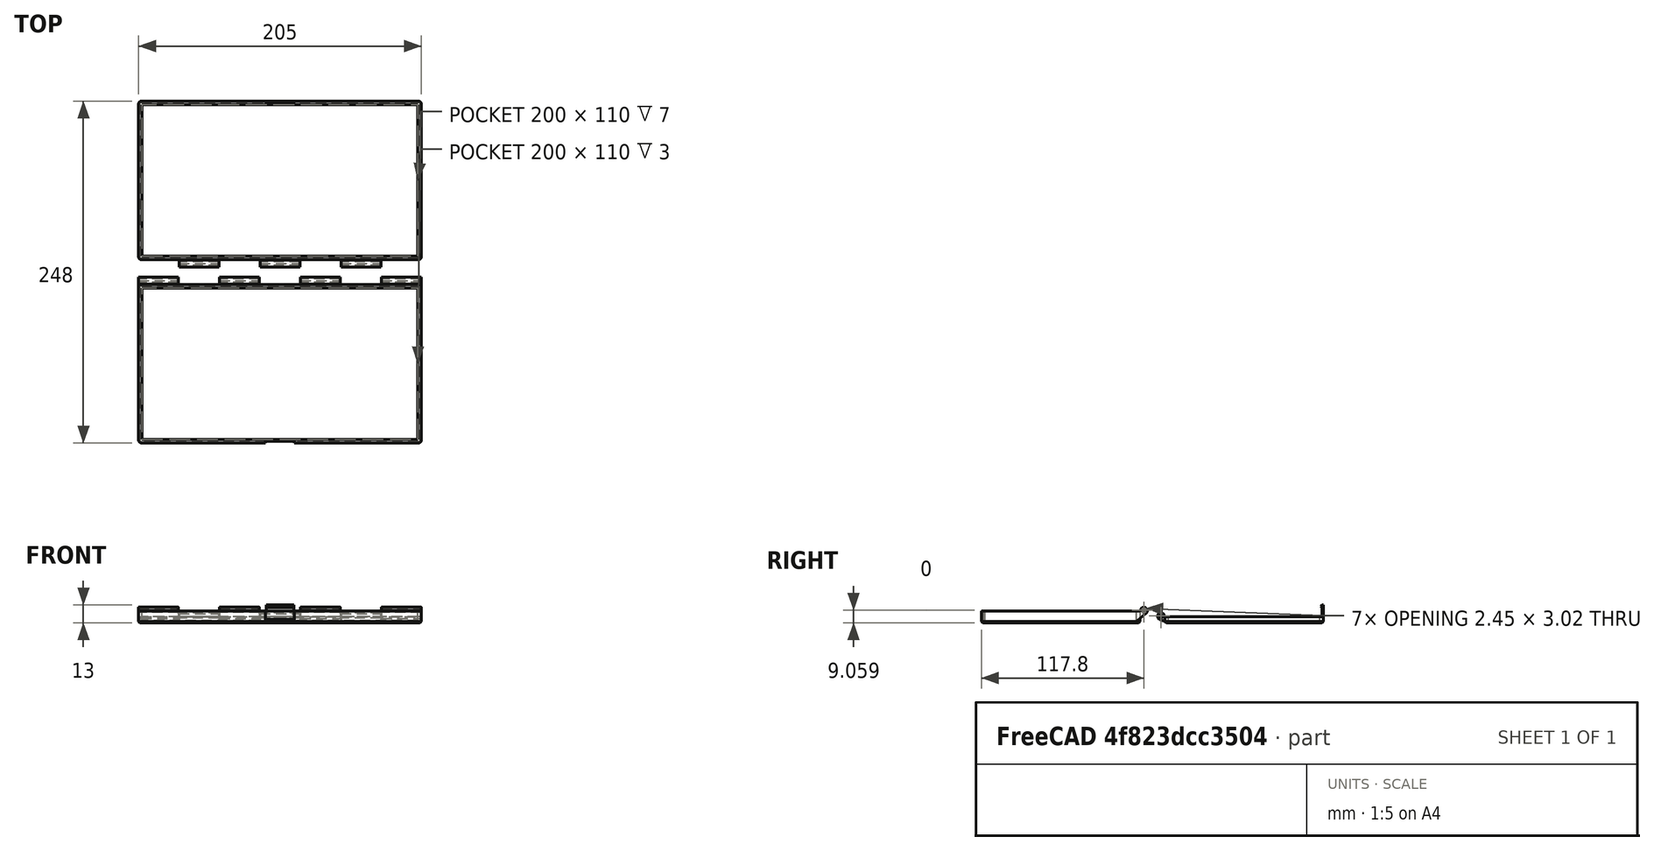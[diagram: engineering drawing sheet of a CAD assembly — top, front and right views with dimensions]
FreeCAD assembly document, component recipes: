
FREECAD ASSEMBLY — COMPONENT RECIPES ("parametric box")

This assembly document has 2 components, labeled P0..P1 below (a component is one placed body or linked part). 2 of them carry a construction recipe — the FreeCAD feature program that regenerates the part from scratch, quoted from this document or its linked companion documents; the rest are supplied as boundary geometry only. No exploded tour is included for this assembly.
COMPONENT P0 — recipe-attached ("bottom", modeled in this document).
Construction recipe (the document's own serialized feature program — sketch geometry with constraints, then the solid features built on it; lengths are millimeters unless a unit is written):

FEATURE [Sketcher::SketchObject] Sketch
  FullyConstrained = true
  MapMode = 5
  Support = -> [XY_Plane]
  expr: Constraints[10] = <<dim>>.depth_plus_walls
  expr: Constraints[9] = <<dim>>.width_plus_walls
  sketch-geometry (4):
    g0: LineSegment StartX=-102.5 StartY=57.5 StartZ=0 EndX=102.5 EndY=57.5 EndZ=0
    g1: LineSegment StartX=102.5 StartY=57.5 StartZ=0 EndX=102.5 EndY=-57.5 EndZ=0
    g2: LineSegment StartX=102.5 StartY=-57.5 StartZ=0 EndX=-102.5 EndY=-57.5 EndZ=0
    g3: LineSegment StartX=-102.5 StartY=-57.5 StartZ=0 EndX=-102.5 EndY=57.5 EndZ=0
  constraints (11):
    c: Coincident(g0,g1)
    c: Coincident(g1,g2)
    c: Coincident(g2,g3)
    c: Coincident(g3,g0)
    c: Horizontal(g0)
    c: Horizontal(g2)
    c: Vertical(g1)
    c: Vertical(g3)
    c: Symmetric(g1,g0,g-1)
    c: DistanceX(g0,g0) = 205
    c: DistanceY(g1,g1) = 115
FEATURE [PartDesign::Pad] Pad
  Direction = (1,1,1)
  Length = 1.5
  Length2 = 100
  Profile = -> Sketch
  Refine = true
  Reversed = true
  Type = 0
  expr: Length = <<dim>>.bottom
FEATURE [Sketcher::SketchObject] Sketch001
  FullyConstrained = true
  MapMode = 5
  Support = -> [XY_Plane]
  expr: Constraints[21] = <<dim>>.wall
  expr: Constraints[20] = <<dim>>.wall
  expr: Constraints[10] = <<dim>>.depth_plus_walls
  expr: Constraints[9] = <<dim>>.width_plus_walls
  sketch-geometry (8):
    g0: LineSegment StartX=-102.5 StartY=57.5 StartZ=0 EndX=102.5 EndY=57.5 EndZ=0
    g1: LineSegment StartX=102.5 StartY=57.5 StartZ=0 EndX=102.5 EndY=-57.5 EndZ=0
    g2: LineSegment StartX=102.5 StartY=-57.5 StartZ=0 EndX=-102.5 EndY=-57.5 EndZ=0
    g3: LineSegment StartX=-102.5 StartY=-57.5 StartZ=0 EndX=-102.5 EndY=57.5 EndZ=0
    g4: LineSegment StartX=-100 StartY=55 StartZ=0 EndX=100 EndY=55 EndZ=0
    g5: LineSegment StartX=100 StartY=55 StartZ=0 EndX=100 EndY=-55 EndZ=0
    g6: LineSegment StartX=100 StartY=-55 StartZ=0 EndX=-100 EndY=-55 EndZ=0
    g7: LineSegment StartX=-100 StartY=-55 StartZ=0 EndX=-100 EndY=55 EndZ=0
  constraints (22):
    c: Coincident(g0,g1)
    c: Coincident(g1,g2)
    c: Coincident(g2,g3)
    c: Coincident(g3,g0)
    c: Horizontal(g0)
    c: Horizontal(g2)
    c: Vertical(g1)
    c: Vertical(g3)
    c: Symmetric(g1,g0,g-1)
    c: DistanceX(g0,g0) = 205
    c: DistanceY(g1,g1) = 115
    c: Coincident(g4,g5)
    c: Coincident(g5,g6)
    c: Coincident(g6,g7)
    c: Coincident(g7,g4)
    c: Horizontal(g4)
    c: Horizontal(g6)
    c: Vertical(g5)
    c: Vertical(g7)
    c: Symmetric(g5,g4,g-1)
    c: DistanceX(g4,g0) = 2.5
    c: DistanceY(g4,g0) = 2.5
FEATURE [PartDesign::Pad] Pad001
  BaseFeature = -> Pad
  Direction = (1,1,1)
  Length = 7
  Length2 = 100
  Profile = -> Sketch001
  Refine = true
  Type = 0
  expr: Length = <<dim>>.height_box
FEATURE [PartDesign::CoordinateSystem] LCS_1
  AttacherType = Attacher::AttachEngine3D
FEATURE [PartDesign::CoordinateSystem] LCS_2
  AttacherType = Attacher::AttachEngine3D
  MapMode = 7
  Placement = pos=(102.5,57.5,7) rot=(0,0.707107,0.707107;3.14159rad)
  Support = -> [Pad001]
FEATURE [Sketcher::SketchObject] Sketch004
  FullyConstrained = true
  MapMode = 5
  Support = -> [XY_Plane]
  expr: Constraints[10] = <<dim>>.lock_thickness + <<dim>>.lock_thick_slack
  expr: Constraints[9] = <<dim>>.lock_width + 2 * <<dim>>.lock_width_slack
  expr: Constraints[7] = -<<dim>>.depth_plus_walls / 2
  sketch-geometry (4):
    g0: LineSegment StartX=-10.4 StartY=-57.5 StartZ=0 EndX=10.4 EndY=-57.5 EndZ=0
    g1: LineSegment StartX=10.4 StartY=-57.5 StartZ=0 EndX=10.4 EndY=-56.3 EndZ=0
    g2: LineSegment StartX=10.4 StartY=-56.3 StartZ=0 EndX=-10.4 EndY=-56.3 EndZ=0
    g3: LineSegment StartX=-10.4 StartY=-56.3 StartZ=0 EndX=-10.4 EndY=-57.5 EndZ=0
  constraints (11):
    c: Coincident(g0,g1)
    c: Coincident(g1,g2)
    c: Coincident(g2,g3)
    c: Coincident(g3,g0)
    c: Horizontal(g2)
    c: Vertical(g1)
    c: Vertical(g3)
    c: DistanceY(g0) = -57.5
    c: Symmetric(g0,g0,g-2)
    c: DistanceX(g0,g0) = 20.8
    c: DistanceY(g1,g1) = 1.2
FEATURE [PartDesign::Pocket] Pocket
  BaseFeature = -> Pad001
  Length = 5
  Length2 = 100
  Midplane = true
  Profile = -> Sketch004
  Refine = true
  Type = 1
FEATURE [Sketcher::SketchObject] Sketch005
  FullyConstrained = true
  MapMode = 5
  Placement = pos=(0,0,0) rot=(0.57735,0.57735,0.57735;2.0944rad)
  Support = -> [YZ_Plane]
  expr: Constraints[6] = -<<dim>>.depth_plus_walls / 2 + <<dim>>.lock_thickness + <<dim>>.lock_thick_slack
  expr: Constraints[8] = <<dim>>.lock_tab
  expr: Constraints[10] = <<dim>>.lock_tab
  expr: Constraints[11] = -<<dim>>.bottom
  sketch-geometry (4):
    g0: LineSegment StartX=-56.3 StartY=-1.5 StartZ=0 EndX=-55.3 EndY=-0.6609 EndZ=0
    g1: LineSegment StartX=-55.3 StartY=-0.6609 StartZ=0 EndX=-55.3 EndY=0.3391 EndZ=0
    g2: LineSegment StartX=-55.3 StartY=0.3391 StartZ=0 EndX=-56.3 EndY=1.1782 EndZ=0
    g3: LineSegment StartX=-56.3 StartY=1.1782 StartZ=0 EndX=-56.3 EndY=-1.5 EndZ=0
  constraints (12):
    c: Coincident(g1,g0)
    c: Vertical(g1)
    c: Coincident(g2,g1)
    c: Coincident(g3,g2)
    c: Vertical(g3)
    c: Coincident(g3,g0)
    c: DistanceX(g0) = -56.3
    c: Angle(g0) = 0.698132
    c: DistanceY(g1,g1) = 1
    c: Angle(g2) = 2.44346
    c: DistanceX(g0,g0) = 1
    c: DistanceY(g0) = -1.5
FEATURE [Sketcher::SketchObject] Sketch008
  AttachmentOffset = pos=(0,0,-102.5) rot=(0,0,1;0rad)
  FullyConstrained = true
  MapMode = 5
  Placement = pos=(-102.5,2.28e-14,-2.28e-14) rot=(0.57735,0.57735,0.57735;2.0944rad)
  Support = -> [YZ_Plane]
  expr: Constraints[26] = <<dim>>.hinge_hole
  expr: Constraints[15] = <<dim>>.height_slack
  expr: Constraints[12] = <<dim>>.hinge_d
  expr: Constraints[11] = <<dim>>.height_slack
  expr: Constraints[10] = <<dim>>.height_box
  expr: Constraints[9] = <<dim>>.depth_plus_walls
  expr: .AttachmentOffset.Base.z = -<<dim>>.width_plus_walls / 2
  sketch-geometry (14):
    g0: Circle CenterX=60.3 CenterY=7.3 CenterZ=0 NormalX=0 NormalY=0 NormalZ=1 AngleXU=0 Radius=2.5
    g1: LineSegment StartX=-57.5 StartY=7 StartZ=0 EndX=57.5 EndY=7 EndZ=0
    g2: LineSegment StartX=57.5 StartY=7 StartZ=0 EndX=57.5 EndY=0 EndZ=0
    g3: LineSegment StartX=57.5 StartY=0 StartZ=0 EndX=-57.5 EndY=0 EndZ=0
    g4: LineSegment StartX=-57.5 StartY=0 StartZ=0 EndX=-57.5 EndY=7 EndZ=0
    g5: GeomPoint X=57.8 Y=7.3 Z=0
    g6: LineSegment StartX=57.5 StartY=7 StartZ=0 EndX=57.8 EndY=7.3 EndZ=0
    g7: LineSegment StartX=61.907 StartY=5.38489 StartZ=0 EndX=57.5 EndY=1.687 EndZ=0
    g8: ArcOfCircle CenterX=60.3 CenterY=7.3 CenterZ=0 NormalX=0 NormalY=0 NormalZ=1 AngleXU=0 Radius=2.5 StartAngle=5.41052 EndAngle=9.42478
    g9: LineSegment StartX=57.5 StartY=7 StartZ=0 EndX=57.5 EndY=1.687 EndZ=0
    g10: Circle CenterX=60.3 CenterY=7.3 CenterZ=0 NormalX=0 NormalY=0 NormalZ=1 AngleXU=0 Radius=1.25
    g11: LineSegment StartX=59.4161 StartY=8.18388 StartZ=0 EndX=60.3 EndY=9.06777 EndZ=0
    g12: LineSegment StartX=60.3 StartY=9.06777 StartZ=0 EndX=61.1839 EndY=8.18389 EndZ=0
    g13: ArcOfCircle CenterX=60.3 CenterY=7.3 CenterZ=0 NormalX=0 NormalY=0 NormalZ=1 AngleXU=0 Radius=1.25 StartAngle=2.3562 EndAngle=7.06859
  constraints (36):
    c: Coincident(g1,g2)
    c: Coincident(g2,g3)
    c: Coincident(g3,g4)
    c: Coincident(g4,g1)
    c: Horizontal(g3)
    c: Vertical(g2)
    c: Vertical(g4)
    c: PointOnObject(g2,g-1)
    c: Symmetric(g1,g1,g-2)
    c: DistanceX(g1,g1) = 115
    c: DistanceY(g2,g2) = 7
    c: DistanceY(g1,g0) = 0.3
    c: Diameter(g0) = 5
    c: PointOnObject(g5,g0)
    c: Horizontal(g5,g0)
    c: DistanceX(g1,g5) = 0.3
    c: Coincident(g6,g1)
    c: Coincident(g6,g5)
    c: PointOnObject(g7,g2)
    c: Angle(g7) = -2.44346
    c: Coincident(g8,g0)
    c: Coincident(g8,g6)
    c: Coincident(g9,g6)
    c: Coincident(g9,g7)
    c: Tangent(g8,g7) = 1.5708
    c: Coincident(g10,g8)
    c: Diameter(g10) = 2.5
    c: PointOnObject(g11,g10)
    c: Tangent(g11,g10)
    c: Coincident(g12,g11)
    c: Tangent(g12,g10)
    c: Vertical(g8,g11)
    c: Coincident(g13,g8)
    c: Coincident(g13,g11)
    c: Coincident(g13,g12)
    c: Perpendicular(g12,g11)
FEATURE [PartDesign::Pocket] Pocket001
  BaseFeature = -> Pocket
  Length = 20.8
  Length2 = 100
  Midplane = true
  Profile = -> Sketch005
  Refine = true
  Type = 0
  expr: Length = <<dim>>.lock_width + 2 * <<dim>>.lock_width_slack
FEATURE [PartDesign::Pad] Pad007
  BaseFeature = -> Pocket001
  Direction = (1,1,1)
  Length = 28.8571
  Length2 = 100
  Profile = -> Sketch008
  Refine = true
  Type = 0
  expr: Length = <<dim>>.hinge_width
FEATURE [PartDesign::LinearPattern] LinearPattern
  BaseFeature = -> Pad007
  Direction = -> X_Axis
  Length = 176.143
  Occurrences = 4
  Originals = -> [Pad007]
  Refine = true
  expr: Occurrences = <<dim>>.num_hinges_bottom
  expr: Length = Spreadsheet.hinge_dist_bottom
FEATURE [PartDesign::Line] HoleAxis_1
  AttacherType = Attacher::AttachEngineLine
  AttachmentOffset = pos=(0,0,0.5) rot=(0,0,1;0rad)
  Length = 2.82656
  MapMode = 19
  Placement = pos=(-73.1429,60.3,7.3) rot=(-0.678598,0.281087,-0.678598;2.59356rad)
  ResizeMode = 1
  Support = -> [Pad007]
  expr: .AttachmentOffset.Base.z = <<dim>>.hinge_spacing
FEATURE [PartDesign::Fillet] Fillet
  Base = -> LinearPattern [Edge43,Edge47,Edge23,Edge19]
  BaseFeature = -> LinearPattern
  Radius = 2
  Refine = true
  SupportTransform = false
  expr: Radius = <<dim>>.vert_fillet
FEATURE [PartDesign::Chamfer] Chamfer
  Angle = 45
  Base = -> Fillet [Edge68]
  BaseFeature = -> Fillet
  ChamferType = 0
  FlipDirection = false
  Size = 1
  Size2 = 1
  SupportTransform = false
  expr: Size = <<dim>>.hor_chamfer
FEATURE [PartDesign::Body] Body  label="bottom"
  Group = -> [Sketch,Pad,Sketch001,Pad001,LCS_1,LCS_2,Sketch004,Pocket,Sketch005,Sketch008,Pocket001,Pad007,LinearPattern,HoleAxis_1,Fillet,Chamfer]
  Origin = -> Origin
  Tip = -> Chamfer
COMPONENT P1 — recipe-attached ("cover", modeled in this document).
Construction recipe (the document's own serialized feature program — sketch geometry with constraints, then the solid features built on it; lengths are millimeters unless a unit is written):

FEATURE [Sketcher::SketchObject] Sketch002
  FullyConstrained = true
  MapMode = 5
  Support = -> [XY_Plane001]
  expr: Constraints[9] = <<dim>>.width_plus_walls
  expr: Constraints[10] = <<dim>>.depth_plus_walls
  sketch-geometry (4):
    g0: LineSegment StartX=-102.5 StartY=57.5 StartZ=0 EndX=102.5 EndY=57.5 EndZ=0
    g1: LineSegment StartX=102.5 StartY=57.5 StartZ=0 EndX=102.5 EndY=-57.5 EndZ=0
    g2: LineSegment StartX=102.5 StartY=-57.5 StartZ=0 EndX=-102.5 EndY=-57.5 EndZ=0
    g3: LineSegment StartX=-102.5 StartY=-57.5 StartZ=0 EndX=-102.5 EndY=57.5 EndZ=0
  constraints (11):
    c: Coincident(g0,g1)
    c: Coincident(g1,g2)
    c: Coincident(g2,g3)
    c: Coincident(g3,g0)
    c: Horizontal(g0)
    c: Horizontal(g2)
    c: Vertical(g1)
    c: Vertical(g3)
    c: Symmetric(g1,g0,g-1)
    c: DistanceX(g0,g0) = 205
    c: DistanceY(g1,g1) = 115
FEATURE [Sketcher::SketchObject] Sketch003
  FullyConstrained = true
  MapMode = 5
  Support = -> [XY_Plane001]
  expr: Constraints[9] = <<dim>>.width_plus_walls
  expr: Constraints[10] = <<dim>>.depth_plus_walls
  expr: Constraints[20] = <<dim>>.wall
  expr: Constraints[21] = <<dim>>.wall
  sketch-geometry (8):
    g0: LineSegment StartX=-102.5 StartY=57.5 StartZ=0 EndX=102.5 EndY=57.5 EndZ=0
    g1: LineSegment StartX=102.5 StartY=57.5 StartZ=0 EndX=102.5 EndY=-57.5 EndZ=0
    g2: LineSegment StartX=102.5 StartY=-57.5 StartZ=0 EndX=-102.5 EndY=-57.5 EndZ=0
    g3: LineSegment StartX=-102.5 StartY=-57.5 StartZ=0 EndX=-102.5 EndY=57.5 EndZ=0
    g4: LineSegment StartX=-100 StartY=55 StartZ=0 EndX=100 EndY=55 EndZ=0
    g5: LineSegment StartX=100 StartY=55 StartZ=0 EndX=100 EndY=-55 EndZ=0
    g6: LineSegment StartX=100 StartY=-55 StartZ=0 EndX=-100 EndY=-55 EndZ=0
    g7: LineSegment StartX=-100 StartY=-55 StartZ=0 EndX=-100 EndY=55 EndZ=0
  constraints (22):
    c: Coincident(g0,g1)
    c: Coincident(g1,g2)
    c: Coincident(g2,g3)
    c: Coincident(g3,g0)
    c: Horizontal(g0)
    c: Horizontal(g2)
    c: Vertical(g1)
    c: Vertical(g3)
    c: Symmetric(g1,g0,g-1)
    c: DistanceX(g0,g0) = 205
    c: DistanceY(g1,g1) = 115
    c: Coincident(g4,g5)
    c: Coincident(g5,g6)
    c: Coincident(g6,g7)
    c: Coincident(g7,g4)
    c: Horizontal(g4)
    c: Horizontal(g6)
    c: Vertical(g5)
    c: Vertical(g7)
    c: Symmetric(g5,g4,g-1)
    c: DistanceX(g4,g0) = 2.5
    c: DistanceY(g4,g0) = 2.5
FEATURE [PartDesign::Pad] Pad003
  Direction = (1,1,1)
  Length = 1.5
  Length2 = 100
  Profile = -> Sketch002
  Refine = true
  Reversed = true
  Type = 0
  expr: Length = <<dim>>.bottom
FEATURE [PartDesign::Pad] Pad002
  BaseFeature = -> Pad003
  Direction = (1,1,1)
  Length = 3
  Length2 = 100
  Profile = -> Sketch003
  Refine = true
  Type = 0
  expr: Length = <<dim>>.height_cover
FEATURE [PartDesign::CoordinateSystem] LCS_3
  AttacherType = Attacher::AttachEngine3D
  MapMode = 7
  Placement = pos=(102.5,-57.5,3) rot=(0,0.707107,0.707107;3.14159rad)
  Support = -> [Pad002]
FEATURE [Sketcher::SketchObject] Sketch006
  AttachmentOffset = pos=(0,0,3) rot=(0,0,1;0rad)
  FullyConstrained = true
  MapMode = 5
  Placement = pos=(0,0,3) rot=(0,0,1;0rad)
  Support = -> [XY_Plane001]
  expr: Constraints[10] = <<dim>>.lock_thickness
  expr: Constraints[9] = <<dim>>.depth_plus_walls / 2
  expr: Constraints[8] = <<dim>>.lock_width
  expr: .AttachmentOffset.Base.z = <<dim>>.height_cover
  sketch-geometry (4):
    g0: LineSegment StartX=-10 StartY=57.5 StartZ=0 EndX=10 EndY=57.5 EndZ=0
    g1: LineSegment StartX=10 StartY=57.5 StartZ=0 EndX=10 EndY=56.5 EndZ=0
    g2: LineSegment StartX=10 StartY=56.5 StartZ=0 EndX=-10 EndY=56.5 EndZ=0
    g3: LineSegment StartX=-10 StartY=56.5 StartZ=0 EndX=-10 EndY=57.5 EndZ=0
  constraints (11):
    c: Coincident(g0,g1)
    c: Coincident(g1,g2)
    c: Coincident(g2,g3)
    c: Coincident(g3,g0)
    c: Horizontal(g2)
    c: Vertical(g1)
    c: Vertical(g3)
    c: Symmetric(g0,g0,g-2)
    c: DistanceX(g0,g0) = 20
    c: DistanceY(g0) = 57.5
    c: DistanceY(g1,g1) = 1
FEATURE [PartDesign::Pad] Pad005
  BaseFeature = -> Pad002
  Direction = (1,1,1)
  Length = 8.5
  Length2 = 100
  Profile = -> Sketch006
  Refine = true
  Type = 0
  expr: Length = <<dim>>.height_box + <<dim>>.bottom
FEATURE [Sketcher::SketchObject] Sketch007
  FullyConstrained = true
  MapMode = 5
  Placement = pos=(0,0,0) rot=(0.57735,0.57735,0.57735;2.0944rad)
  Support = -> [YZ_Plane001]
  expr: Constraints[2] = <<dim>>.lock_tab
  expr: Constraints[1] = <<dim>>.depth_plus_walls / 2 - <<dim>>.lock_thickness
  expr: Constraints[0] = <<dim>>.height_cover + <<dim>>.height_box + <<dim>>.bottom
  sketch-geometry (3):
    g0: LineSegment StartX=56.5 StartY=11.5 StartZ=0 EndX=55.5 EndY=10.5 EndZ=0
    g1: LineSegment StartX=55.5 StartY=10.5 StartZ=0 EndX=56.5 EndY=9.5 EndZ=0
    g2: LineSegment StartX=56.5 StartY=9.5 StartZ=0 EndX=56.5 EndY=11.5 EndZ=0
  constraints (9):
    c: DistanceY(g0) = 11.5
    c: DistanceX(g0) = 56.5
    c: DistanceX(g0,g0) = 1
    c: Angle(g0) = -2.35619
    c: Coincident(g1,g0)
    c: Coincident(g2,g1)
    c: Coincident(g2,g0)
    c: Vertical(g2)
    c: Equal(g1,g0)
FEATURE [PartDesign::Pad] Pad006
  BaseFeature = -> Pad005
  Direction = (1,1,1)
  Length = 20
  Length2 = 100
  Midplane = true
  Profile = -> Sketch007
  Refine = true
  Type = 0
  expr: Length = <<dim>>.lock_width
FEATURE [Sketcher::SketchObject] Sketch009
  AttachmentOffset = pos=(0,0,-73.1429) rot=(0,0,1;0rad)
  FullyConstrained = true
  MapMode = 5
  Placement = pos=(-73.1429,1.62e-14,-1.62e-14) rot=(0.57735,0.57735,0.57735;2.0944rad)
  Support = -> [YZ_Plane001]
  expr: Constraints[26] = <<dim>>.top - <<dim>>.hor_chamfer - 0.01
  expr: Constraints[16] = <<dim>>.height_slack
  expr: Constraints[15] = <<dim>>.hinge_hole
  expr: Constraints[10] = <<dim>>.height_cover
  expr: Constraints[17] = <<dim>>.height_slack
  expr: Constraints[9] = <<dim>>.depth_plus_walls
  expr: Constraints[13] = <<dim>>.hinge_d
  expr: .AttachmentOffset.Base.z = -<<dim>>.width_plus_walls / 2 + <<dim>>.hinge_width + <<dim>>.hinge_spacing
  sketch-geometry (14):
    g0: LineSegment StartX=57.5 StartY=0 StartZ=0 EndX=-57.5 EndY=0 EndZ=0
    g1: LineSegment StartX=-57.5 StartY=0 StartZ=0 EndX=-57.5 EndY=3 EndZ=0
    g2: LineSegment StartX=-57.5 StartY=3 StartZ=0 EndX=57.5 EndY=3 EndZ=0
    g3: LineSegment StartX=57.5 StartY=3 StartZ=0 EndX=57.5 EndY=0 EndZ=0
    g4: Circle CenterX=-60.3 CenterY=3.3 CenterZ=0 NormalX=0 NormalY=0 NormalZ=1 AngleXU=0 Radius=2.5
    g5: GeomPoint X=-57.8 Y=3.3 Z=0
    g6: Circle CenterX=-60.3 CenterY=3.3 CenterZ=0 NormalX=0 NormalY=0 NormalZ=1 AngleXU=0 Radius=1.25
    g7: LineSegment StartX=-57.5 StartY=3 StartZ=0 EndX=-57.8 EndY=3.3 EndZ=0
    g8: LineSegment StartX=-57.5 StartY=3 StartZ=0 EndX=-57.5 EndY=-0.49 EndZ=0
    g9: LineSegment StartX=-57.5 StartY=-0.49 StartZ=0 EndX=-61.2163 EndY=0.973974 EndZ=0
    g10: ArcOfCircle CenterX=-60.3 CenterY=3.3 CenterZ=0 NormalX=0 NormalY=0 NormalZ=1 AngleXU=0 Radius=2.5 StartAngle=0 EndAngle=4.33712
    g11: LineSegment StartX=-61.1839 StartY=4.18389 StartZ=0 EndX=-60.3 EndY=5.06777 EndZ=0
    g12: LineSegment StartX=-60.3 StartY=5.06777 StartZ=0 EndX=-59.4161 EndY=4.18387 EndZ=0
    g13: ArcOfCircle CenterX=-60.3 CenterY=3.3 CenterZ=0 NormalX=0 NormalY=0 NormalZ=1 AngleXU=0 Radius=1.25 StartAngle=2.35619 EndAngle=7.06857
  constraints (36):
    c: Coincident(g0,g1)
    c: Coincident(g1,g2)
    c: Coincident(g2,g3)
    c: Coincident(g3,g0)
    c: Horizontal(g0)
    c: Vertical(g1)
    c: Vertical(g3)
    c: PointOnObject(g0,g-1)
    c: Symmetric(g2,g1,g-2)
    c: DistanceX(g2,g2) = 115
    c: DistanceY(g1,g1) = 3
    c: PointOnObject(g5,g4)
    c: Horizontal(g5,g4)
    c: Diameter(g4) = 5
    c: Coincident(g6,g4)
    c: Diameter(g6) = 2.5
    c: DistanceX(g5,g1) = 0.3
    c: DistanceY(g1,g5) = 0.3
    c: Coincident(g7,g1)
    c: Coincident(g7,g5)
    c: Coincident(g8,g7)
    c: Vertical(g8)
    c: Coincident(g9,g8)
    c: Coincident(g10,g6)
    c: Coincident(g10,g7)
    c: Tangent(g10,g9) = 1.5708
    c: DistanceY(g8,g0) = 0.49
    c: PointOnObject(g11,g6)
    c: Tangent(g11,g6)
    c: Coincident(g12,g11)
    c: Tangent(g12,g6)
    c: Coincident(g13,g10)
    c: Coincident(g13,g11)
    c: Coincident(g13,g12)
    c: Perpendicular(g12,g11)
    c: Vertical(g11,g10)
FEATURE [PartDesign::Pad] Pad008
  BaseFeature = -> Pad006
  Direction = (1,1,1)
  Length = 28.8571
  Length2 = 100
  Profile = -> Sketch009
  Refine = true
  Type = 0
  expr: Length = <<dim>>.hinge_width
FEATURE [PartDesign::LinearPattern] LinearPattern001
  BaseFeature = -> Pad008
  Direction = -> X_Axis001
  Length = 117.429
  Occurrences = 3
  Originals = -> [Pad008]
  Refine = true
  expr: Occurrences = <<dim>>.num_hinges_cover
  expr: Length = <<dim>>.hinge_dist_cover
FEATURE [PartDesign::Line] HoleAxis_2
  AttacherType = Attacher::AttachEngineLine
  Length = 2.82656
  MapMode = 19
  Placement = pos=(-73.1429,-60.3,3.3) rot=(-0.678599,0.281081,-0.678599;2.59357rad)
  ResizeMode = 1
  Support = -> [Pad008]
FEATURE [PartDesign::Fillet] Fillet001
  Base = -> LinearPattern001 [Edge32,Edge42,Edge20,Edge19]
  BaseFeature = -> LinearPattern001
  Radius = 2
  Refine = true
  SupportTransform = false
  expr: Radius = <<dim>>.vert_fillet
FEATURE [PartDesign::Chamfer] Chamfer001
  Angle = 45
  Base = -> Fillet001 [Face20]
  BaseFeature = -> Fillet001
  ChamferType = 0
  FlipDirection = false
  Refine = true
  Size = 1
  Size2 = 1
  SupportTransform = false
  expr: Size = <<dim>>.hor_chamfer
FEATURE [PartDesign::Body] Body001  label="cover"
  Group = -> [Sketch002,Pad003,Sketch003,Pad002,LCS_3,Sketch006,Pad005,Sketch007,Pad006,Sketch009,Pad008,LinearPattern001,HoleAxis_2,Fillet001,Chamfer001]
  Origin = -> Origin001
  Placement = pos=(0,133,0) rot=(0,0,1;0rad)
  Tip = -> Chamfer001
PROVENANCE & LICENSES
A FreeCAD (.FCStd) document from a public repository crawl; recipes are the document's own serialized feature recipes (and, for linked parts, companion documents' recipes).
License: as declared in the source repository (recorded in the dataset sidecar).
